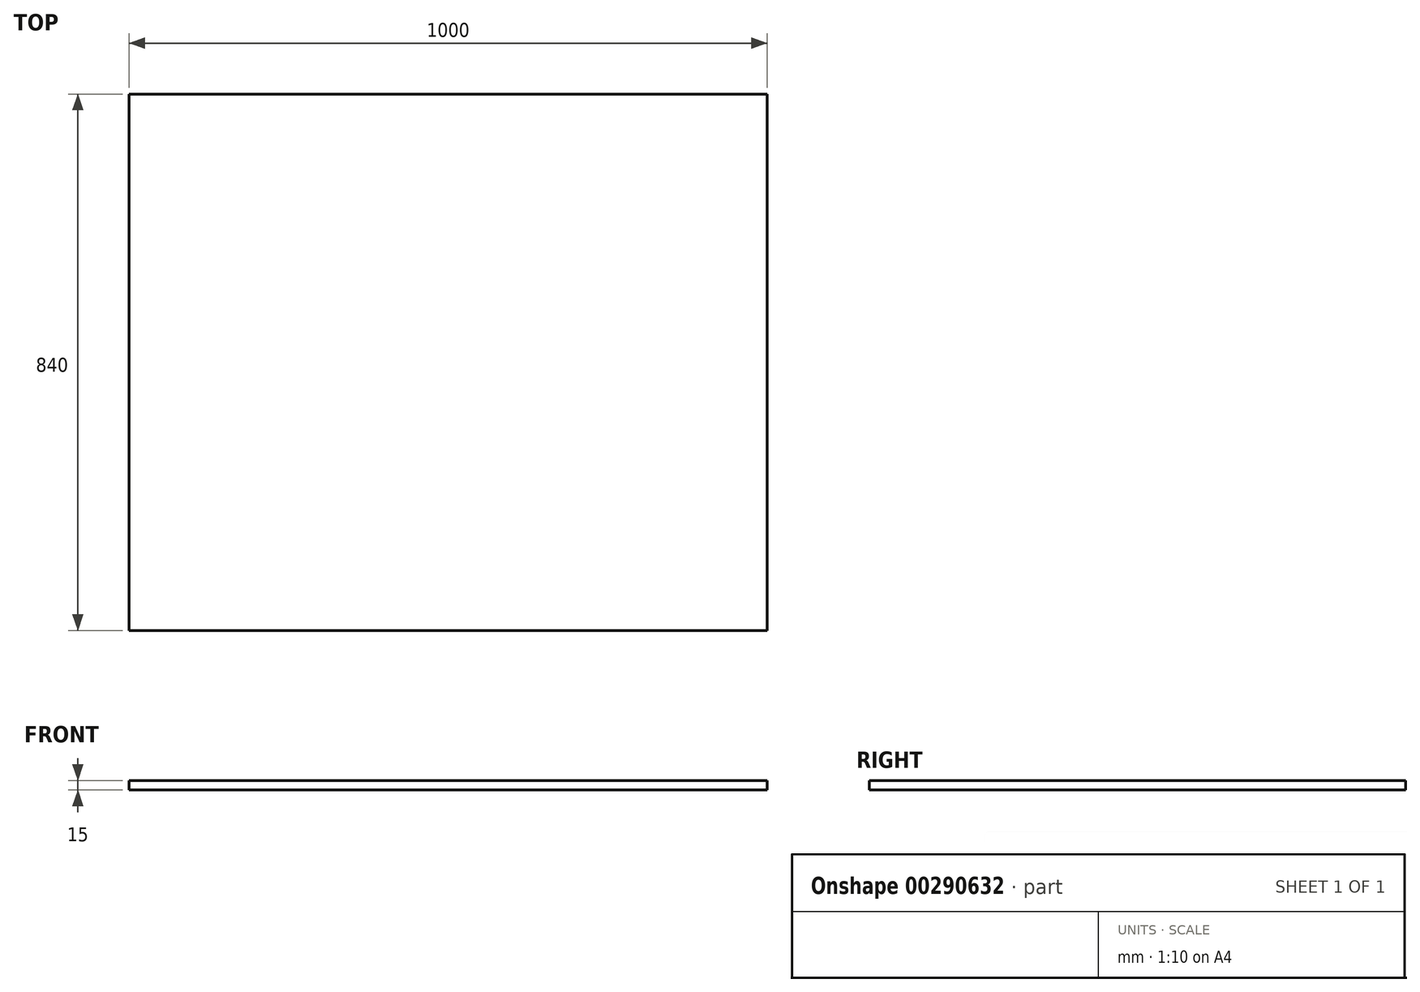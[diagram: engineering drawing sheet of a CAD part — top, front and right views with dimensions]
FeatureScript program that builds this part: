
annotation { "Feature Type Name" : "Feature", "Feature Type Description" : "" }
export const myFeature = defineFeature(function(context is Context, id is Id, definition is map)
    precondition{}
    {
        {
            var Q0;
            Q0=qCreatedBy(makeId("Top.planeOp"),FACE);
            var sketch = newSketch(context, id + "F0", { "sketchPlane" : qUnion([Q0])});
            skLineSegment(sketch, "E0.bottom", {"start": v(-500, 420) * mm, "end": v(500, 420) * mm});
            skLineSegment(sketch, "E0.top", {"start": v(-500, -420) * mm, "end": v(500, -420) * mm});
            skLineSegment(sketch, "E0.left", {"start": v(-500, 420) * mm, "end": v(-500, -420) * mm});
            skLineSegment(sketch, "E0.right", {"start": v(500, 420) * mm, "end": v(500, -420) * mm});
            skLineSegment(sketch, "E1", {"start": v(0, 420) * mm, "end": v(0, -420) * mm, "construction": true});
            skLineSegment(sketch, "E2", {"start": v(-500, 0) * mm, "end": v(500, 0) * mm, "construction": true});
            skLineSegment(sketch, "E3", {"start": v(-500, 100) * mm, "end": v(500, 100) * mm, "construction": true});
            skLineSegment(sketch, "E4.MirrorCS", {"start": v(-500, -100) * mm, "end": v(500, -100) * mm, "construction": true});
            skLineSegment(sketch, "E5", {"start": v(-100, 420) * mm, "end": v(-100, 100) * mm});
            skLineSegment(sketch, "E6.trimOffspring", {"start": v(-190, 0) * mm, "end": v(-190, -420) * mm, "construction": true});
            skLineSegment(sketch, "E7.trimOffspring", {"start": v(190, 0) * mm, "end": v(190, -420) * mm, "construction": true});
            skPoint(sketch, "E8.MirrorCS.start.orphan", {"position": v(100, 420) * mm});
            skLineSegment(sketch, "E9.MirrorCS", {"start": v(100, 420) * mm, "end": v(100, 100) * mm});
            skLineSegment(sketch, "E10.MirrorCS", {"start": v(-100, -420) * mm, "end": v(-100, -100) * mm});
            skLineSegment(sketch, "E11.MirrorCS", {"start": v(100, -420) * mm, "end": v(100, -100) * mm});
            skSolve(sketch);
        }
        {
            var Q0;
            Q0 = qSketchRegion(id + "F0", true);
            extrude(context, id + "F1", {"entities" : qUnion([Q0]), "depth" : 15 * mm});
        }
    });
